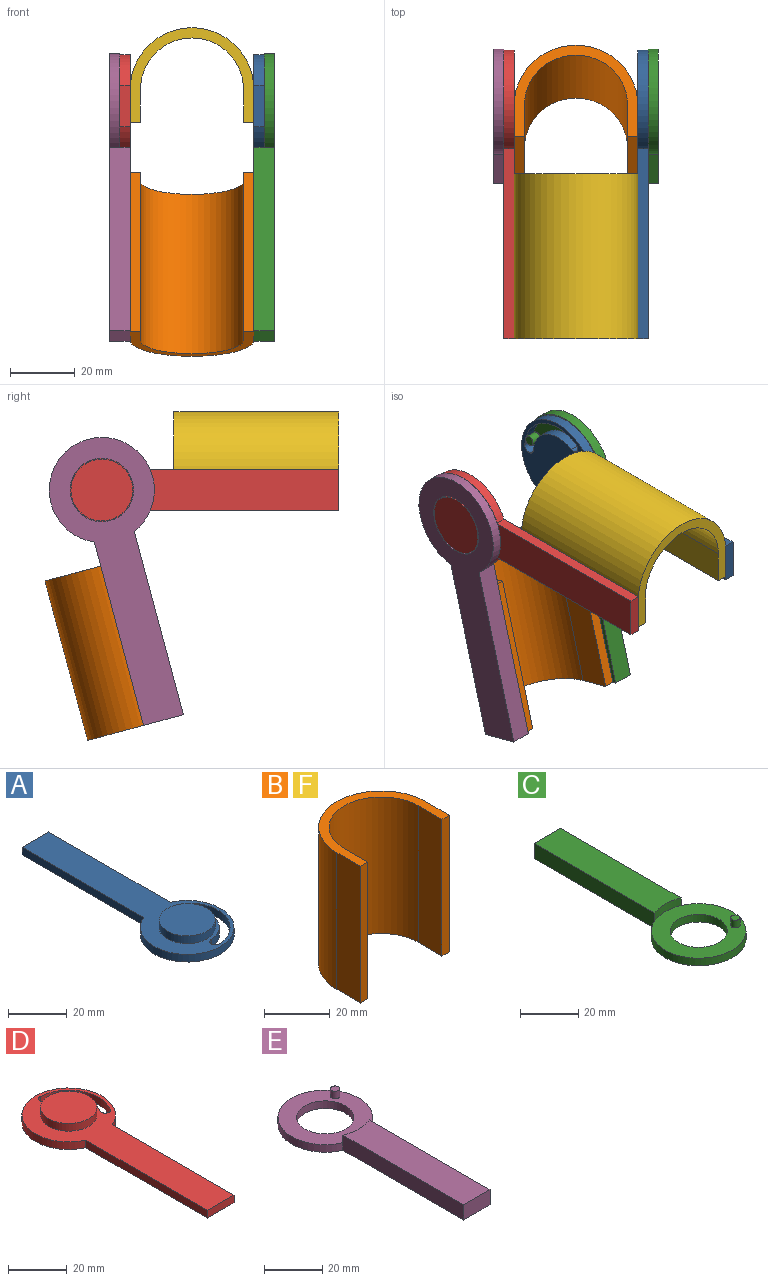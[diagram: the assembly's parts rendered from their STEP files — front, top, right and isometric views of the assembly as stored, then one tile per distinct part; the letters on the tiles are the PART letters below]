
ASSEMBLY  parts=6 mates=5
PART A: 12 faces, bbox 31.8x88.9x6.4 mm
  f0: plane 58.48x3.18mm, normal (1,0,0), area 185.7mm2, adj f1,f3,f4,f9
  f1: plane 12.7x3.18mm, normal (0,1,0), area 40.3mm2, adj f0,f2,f3,f4
  f2: plane 58.48x3.18mm, normal (-1,0,0), area 185.7mm2, adj f1,f3,f4,f9
  f3: plane 88.9x31.75mm, normal (0,0,1), area 1130.7mm2, adj f0,f1,f2,f5,f6,f7,f8,f9
  f4: plane 88.9x31.75mm, normal (0,0,-1), area 1415.8mm2, adj f0,f1,f2,f5,f6,f7,f8,f9
  f5: cylinder r=1.84mm len=3.41mm, axis (0,0,-1), area 18.4mm2, adj f3,f4,f6,f8
  f6: cylinder r=14.54mm len=22.16mm, axis (0,0,-1), area 95.4mm2, adj f3,f4,f5,f7
  f7: cylinder r=1.84mm len=3.68mm, axis (0,0,-1), area 18.4mm2, adj f3,f4,f6,f8
  f8: cylinder r=10.86mm len=16.54mm, axis (0,0,-1), area 71.2mm2, adj f3,f4,f5,f7
  f9: cylinder r=15.88mm len=31.75mm, axis (0,0,-1), area 275.2mm2, adj f0,f2,f3,f4
  f10: cylinder r=9.53mm len=19.05mm, axis (0,0,-1), area 190mm2, adj f3,f11
  f11: plane 19.05x19.05mm, normal (0,0,1), area 285mm2, adj f10
PART B: 10 faces, bbox 38.1x29.2x50.8 mm
  f0: cylinder r=19.05mm len=50.8mm, axis (0,0,-1), area 3040.2mm2, adj f1,f7,f8,f9
  f1: plane 50.8x10.16mm, normal (-1,0,0), area 516.1mm2, adj f0,f2,f8,f9
  f2: plane 50.8x3.18mm, normal (0,-1,0), area 161.3mm2, adj f1,f3,f8,f9
  f3: plane 50.8x10.16mm, normal (1,0,0), area 516.1mm2, adj f2,f4,f8,f9
  f4: cylinder r=15.88mm len=50.8mm, axis (0,0,-1), area 2533.5mm2, adj f3,f5,f8,f9
  f5: plane 50.8x10.16mm, normal (-1,0,0), area 516.1mm2, adj f4,f6,f8,f9
  f6: plane 50.8x3.18mm, normal (0,-1,0), area 161.3mm2, adj f5,f7,f8,f9
  f7: plane 50.8x10.16mm, normal (1,0,0), area 516.1mm2, adj f0,f6,f8,f9
  f8: plane 38.1x29.21mm, normal (0,0,1), area 238.7mm2, adj f0,f1,f2,f3,f4,f5,f6,f7
  f9: plane 38.1x29.21mm, normal (0,0,-1), area 238.7mm2, adj f0,f1,f2,f3,f4,f5,f6,f7
PART C: 11 faces, bbox 32.4x89.6x6.4 mm
  f0: cylinder r=16.19mm len=12.7mm, axis (0,0,-1), area 41.4mm2, adj f1,f3,f4,f8
  f1: plane 58.48x6.35mm, normal (1,0,0), area 371.3mm2, adj f0,f2,f4,f5,f6
  f2: plane 12.7x6.35mm, normal (0,1,0), area 80.6mm2, adj f1,f3,f4,f5
  f3: plane 58.48x6.35mm, normal (-1,0,0), area 371.3mm2, adj f0,f2,f4,f5,f6
  f4: plane 58.48x12.7mm, normal (0,0,1), area 731.6mm2, adj f0,f1,f2,f3
  f5: plane 89.56x32.39mm, normal (0,0,-1), area 1254.9mm2, adj f1,f2,f3,f6,f7
  f6: cylinder r=16.19mm len=32.39mm, axis (0,0,-1), area 281.6mm2, adj f1,f3,f5,f8
  f7: cylinder r=9.78mm len=19.56mm, axis (0,0,-1), area 195.1mm2, adj f5,f8
  f8: plane 32.39x32.39mm, normal (0,0,1), area 515.4mm2, adj f0,f6,f7,f9
  f9: cylinder r=1.59mm len=3.18mm, axis (0,0,-1), area 31.7mm2, adj f8,f10
  f10: plane 3.18x3.18mm, normal (0,0,1), area 7.9mm2, adj f9
PART D: 12 faces, bbox 31.8x88.9x6.4 mm
  f0: plane 58.48x3.18mm, normal (1,0,0), area 185.7mm2, adj f1,f3,f4,f9
  f1: plane 12.7x3.18mm, normal (0,-1,0), area 40.3mm2, adj f0,f2,f3,f4
  f2: plane 58.48x3.18mm, normal (-1,0,0), area 185.7mm2, adj f1,f3,f4,f9
  f3: plane 88.9x31.75mm, normal (0,0,1), area 1130.7mm2, adj f0,f1,f2,f5,f6,f7,f8,f9
  f4: plane 88.9x31.75mm, normal (0,0,-1), area 1415.8mm2, adj f0,f1,f2,f5,f6,f7,f8,f9
  f5: cylinder r=1.84mm len=3.41mm, axis (0,0,-1), area 18.4mm2, adj f3,f4,f6,f8
  f6: cylinder r=14.54mm len=22.16mm, axis (0,0,-1), area 95.4mm2, adj f3,f4,f5,f7
  f7: cylinder r=1.84mm len=3.68mm, axis (0,0,-1), area 18.4mm2, adj f3,f4,f6,f8
  f8: cylinder r=10.86mm len=16.54mm, axis (0,0,-1), area 71.2mm2, adj f3,f4,f5,f7
  f9: cylinder r=15.88mm len=31.75mm, axis (0,0,-1), area 275.2mm2, adj f0,f2,f3,f4
  f10: cylinder r=9.53mm len=19.05mm, axis (0,0,-1), area 190mm2, adj f3,f11
  f11: plane 19.05x19.05mm, normal (0,0,1), area 285mm2, adj f10
PART E: 11 faces, bbox 32.4x89.6x6.4 mm
  f0: cylinder r=16.19mm len=12.7mm, axis (0,0,-1), area 41.4mm2, adj f1,f3,f4,f8
  f1: plane 58.48x6.35mm, normal (1,0,0), area 371.3mm2, adj f0,f2,f4,f5,f6
  f2: plane 12.7x6.35mm, normal (0,-1,0), area 80.6mm2, adj f1,f3,f4,f5
  f3: plane 58.48x6.35mm, normal (-1,0,0), area 371.3mm2, adj f0,f2,f4,f5,f6
  f4: plane 58.48x12.7mm, normal (0,0,1), area 731.6mm2, adj f0,f1,f2,f3
  f5: plane 89.56x32.39mm, normal (0,0,-1), area 1254.9mm2, adj f1,f2,f3,f6,f7
  f6: cylinder r=16.19mm len=32.39mm, axis (0,0,-1), area 281.6mm2, adj f1,f3,f5,f8
  f7: cylinder r=9.78mm len=19.56mm, axis (0,0,-1), area 195.1mm2, adj f5,f8
  f8: plane 32.39x32.39mm, normal (0,0,1), area 515.4mm2, adj f0,f6,f7,f9
  f9: cylinder r=1.59mm len=3.18mm, axis (0,0,-1), area 31.7mm2, adj f8,f10
  f10: plane 3.18x3.18mm, normal (0,0,1), area 7.9mm2, adj f9
PART F: same geometry as B
PLACE A rot(axis=(0.71,0,0.71),180deg) t=(0,73.03,-25.4)mm
PLACE B rot(axis=(-1,0,0),15deg) t=(19.05,49.13,-69.56)mm
PLACE C rot(axis=(-0.62,-0.48,0.62),129deg) t=(6.35,11.69,16.44)mm
PLACE D rot(axis=(0,-1,0),90deg) t=(-38.1,111.12,-25.4)mm
PLACE E rot(axis=(0.52,0.68,0.52),111.8deg) t=(-44.45,21.55,53.24)mm
PLACE F rot(axis=(1,0,0),90deg) t=(19.05,50.8,-5.08)mm
MATE fastened B.f7 <-> C.f4  axis (1,0,0) through (0,54.04,-70.87)mm
MATE fastened F.f7 <-> A.f4  axis (1,0,0) through (0,0,0)mm
MATE fastened B.f1 <-> E.f4  axis (-1,0,0) through (-38.1,54.04,-70.87)mm
MATE fastened D.f4 <-> F.f1  axis (1,0,0) through (-38.1,0,0)mm
MATE revolute C.f0 <-> A.f6  axis (-1,0,0) through (3.18,73.02,0)mm
